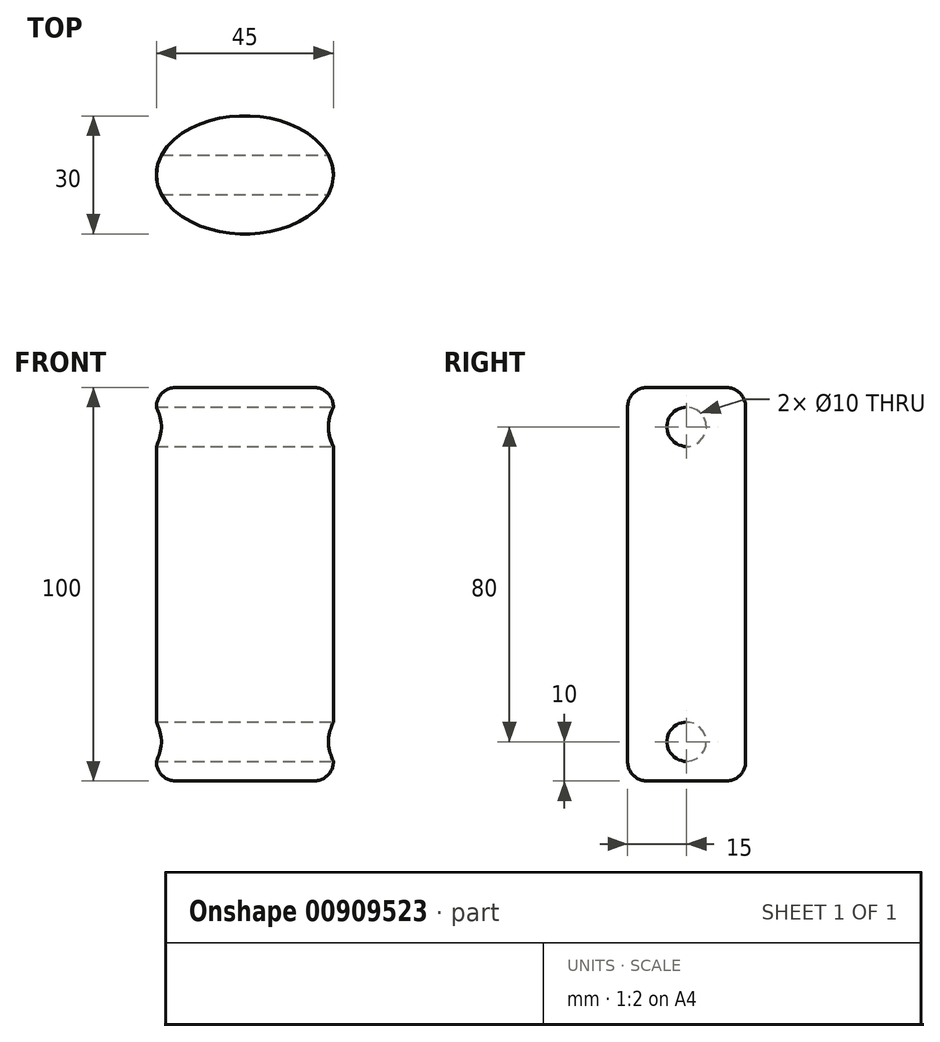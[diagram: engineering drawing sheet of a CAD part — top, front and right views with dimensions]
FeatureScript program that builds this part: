
annotation { "Feature Type Name" : "Feature", "Feature Type Description" : "" }
export const myFeature = defineFeature(function(context is Context, id is Id, definition is map)
    precondition{}
    {
        {
            var Q0;
            Q0=qCreatedBy(makeId("Top.planeOp"),FACE);
            var sketch = newSketch(context, id + "F0", { "sketchPlane" : qUnion([Q0])});
            skEllipse(sketch, "E0", {"center": v(0, 0) * mm, "majorRadius": 15 * mm, "minorRadius": 22.5 * mm, "majorAxis": v(0, -1)});
            skSolve(sketch);
        }
        {
            var Q0;
            Q0=makeQuery(id+"F0.imprint","IMPRINT",FACE,{"disambiguationData":[TD([[makeQuery(id+"F0.imprint","IMPRINT",EDGE,{"derivedFrom":sQuery(id+"F0.wireOp",EDGE,"E0")}),1.0]])]});
            extrude(context, id + "F1", {"entities" : qUnion([Q0]), "depth" : 100 * mm, "offsetDistance" : 25 * mm});
        }
        {
            var Q0;
            Q0=qCreatedBy(makeId("Right.planeOp"),FACE);
            var sketch = newSketch(context, id + "F2", { "sketchPlane" : qUnion([Q0])});
            skCircle(sketch, "E1", {"center": v(0, 90) * mm, "radius": 5 * mm});
            skCircle(sketch, "E2", {"center": v(0, 10) * mm, "radius": 5 * mm});
            skSolve(sketch);
        }
        {
            var Q0;
            Q0 = qSketchRegion(id + "F2", true);
            extrude(context, id + "F3", {"entities" : qUnion([Q0]), "operationType" : NewBodyOperationType.REMOVE, "endBound" : BoundingType.SYMMETRIC, "oppositeDirection" : true, "depth" : 50 * mm, "offsetDistance" : 25 * mm});
        }
        {
            var Q0;
            Q0=makeQuery(id+"F1.opExtrude","CAP_FACE",FACE,{"disambiguationData":[OSD([sQuery(id+"F0.wireOp",EDGE,"E0")])],"isStart":false});
            var Q1;
            Q1=makeQuery(id+"F1.opExtrude","CAP_FACE",FACE,{"disambiguationData":[OSD([sQuery(id+"F0.wireOp",EDGE,"E0")])],"isStart":true});
            fillet(context, id + "F4", {"entities" : qUnion([Q0, Q1]), "radius" : 5 * mm, "tangentPropagation" : true, "allowEdgeOverflow" : false});
        }
    });
